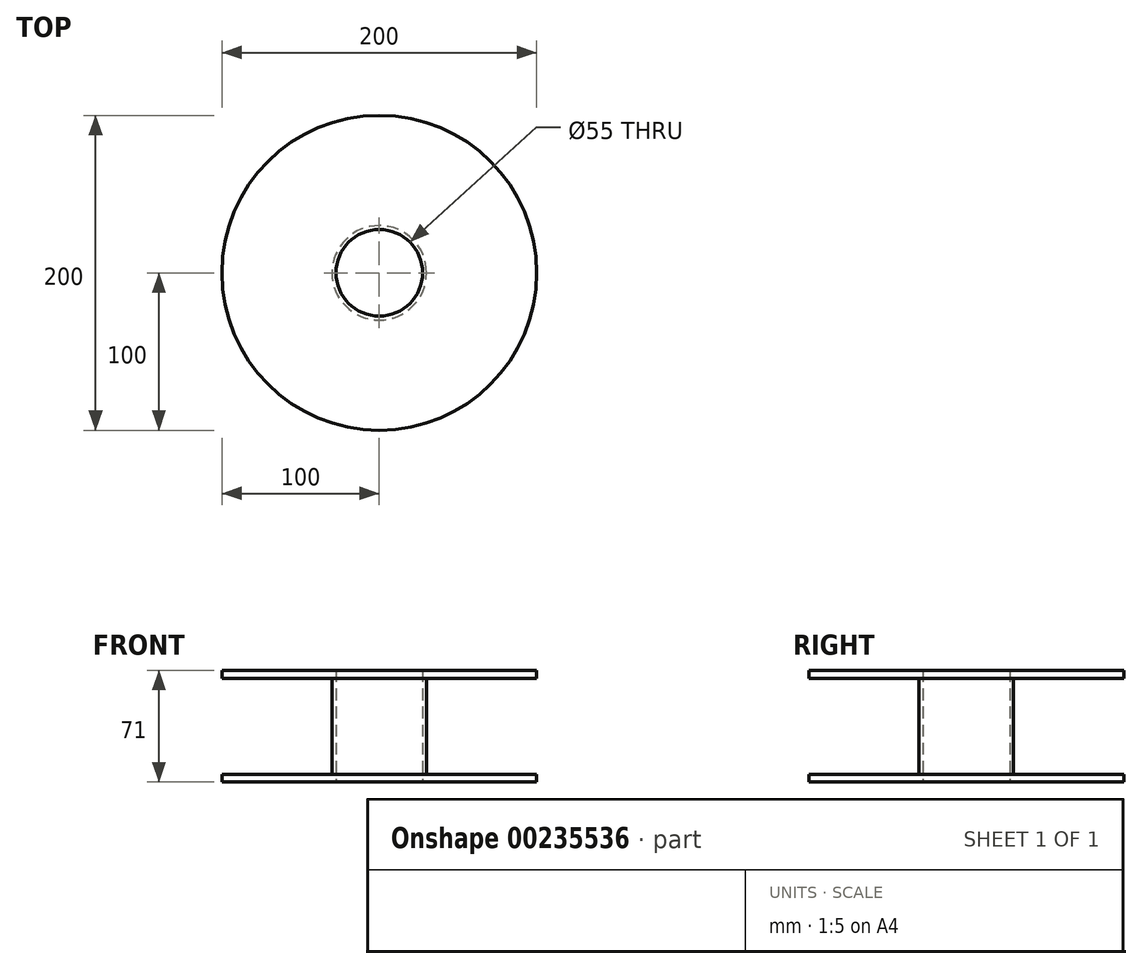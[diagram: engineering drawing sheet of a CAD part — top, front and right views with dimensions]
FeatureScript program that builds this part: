
annotation { "Feature Type Name" : "Feature", "Feature Type Description" : "" }
export const myFeature = defineFeature(function(context is Context, id is Id, definition is map)
    precondition{}
    {
        {
            var Q0;
            Q0=qCreatedBy(makeId("Top.planeOp"),FACE);
            var sketch = newSketch(context, id + "F0", { "sketchPlane" : qUnion([Q0])});
            skCircle(sketch, "E0", {"center": v(0, 0) * mm, "radius": 100 * mm});
            skCircle(sketch, "E1", {"center": v(0, 0) * mm, "radius": 30 * mm});
            skCircle(sketch, "E2", {"center": v(0, 0) * mm, "radius": 27.5 * mm});
            skSolve(sketch);
        }
        {
            var Q0;
            Q0 = qSketchRegion(id + "F0", true);
            extrude(context, id + "F1", {"entities" : qUnion([Q0]), "depth" : 5 * mm});
        }
        {
            var Q0;
            Q0=makeQuery(id+"F0.imprint","IMPRINT",FACE,{"disambiguationData":[TD([[makeQuery(id+"F0.imprint","IMPRINT",EDGE,{"derivedFrom":sQuery(id+"F0.wireOp",EDGE,"E1")}),1.0]])]});
            extrude(context, id + "F2", {"entities" : qUnion([Q0]), "operationType" : NewBodyOperationType.ADD, "depth" : 5 * mm, "hasSecondDirection" : true, "secondDirectionOppositeDirection" : true, "secondDirectionDepth" : 66 * mm});
        }
        {
            var Q0;
            Q0=makeQuery(id+"F0.imprint","IMPRINT",FACE,{"disambiguationData":[TD([[makeQuery(id+"F0.imprint","IMPRINT",EDGE,{"derivedFrom":sQuery(id+"F0.wireOp",EDGE,"E0")}),1.0]])]});
            extrude(context, id + "F3", {"entities" : qUnion([Q0]), "operationType" : NewBodyOperationType.ADD, "oppositeDirection" : true, "depth" : 66 * mm, "hasSecondDirection" : true, "secondDirectionOppositeDirection" : true, "secondDirectionDepth" : 61 * mm});
        }
    });
